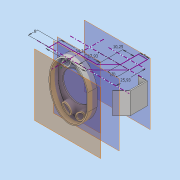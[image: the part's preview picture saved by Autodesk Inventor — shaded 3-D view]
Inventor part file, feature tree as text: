
AUTODESK INVENTOR PART (.ipt)
format: ipt  version: 2019 (Build 230136000, 136)  size: 237,056 bytes
history: native  units: mm
features: other x8, extrude x4, shell x3, sketch x3
ambient origin geometry x8: Origin, YZ Plane, XZ Plane, XY Plane, X Axis, Y Axis, Z Axis, Center Point
bodies: Body1 (feature_tree), Body2 (feature_tree), Body3 (feature_tree)
feature tree (18):
  other  "Твердое тело1"
  extrude  "Выдавливание1"  Depth=34.31mm
  other  "РабПлоскость4"
  extrude  "Круг"  Depth=8.0mm
  shell  "сам корпус"  Thickness=34.31mm
  shell  "Для круга"  Thickness=8.0mm
  other  "РабПлоскость8"
  extrude  "Выдавливание4"  Depth=17.93mm
  other  "РабПлоскость11"
  other  "Дыры в корпусе"
  extrude  "Выдавливание5"  Depth=25.93mm
  shell  "Оболочка5"  Thickness=10.25mm
  other  "Удаление грани1"
  sketch  "Эскиз1"
  sketch  "Эскиз7"
  other  "Элипс"
  sketch  "Эскиз12"
  other  "Твердое тело4"
